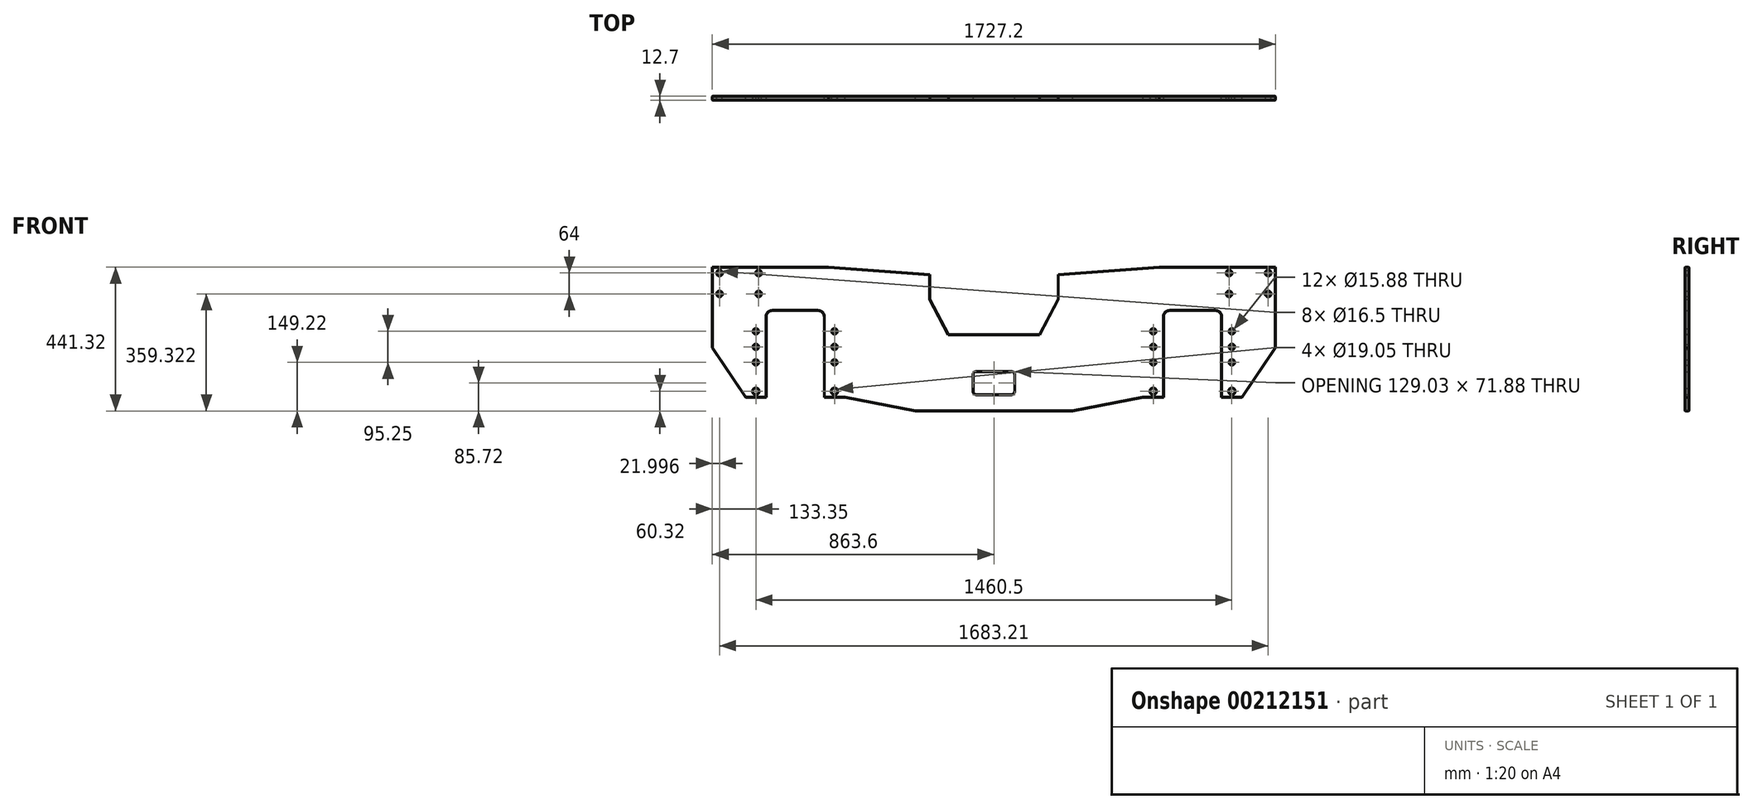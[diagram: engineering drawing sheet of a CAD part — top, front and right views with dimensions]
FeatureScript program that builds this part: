
annotation { "Feature Type Name" : "Feature", "Feature Type Description" : "" }
export const myFeature = defineFeature(function(context is Context, id is Id, definition is map)
    precondition{}
    {
        {
            var Q0;
            Q0=qCreatedBy(makeId("Front.planeOp"),FACE);
            var sketch = newSketch(context, id + "F0", { "sketchPlane" : qUnion([Q0])});
            skLineSegment(sketch, "E0", {"start": v(0, 0) * mm, "end": v(0, 247.15) * mm});
            skLineSegment(sketch, "E1", {"start": v(0, 247.15) * mm, "end": v(355.6, 247.15) * mm});
            skLineSegment(sketch, "E2", {"start": v(355.6, 247.15) * mm, "end": v(666.75, 224.93) * mm});
            skLineSegment(sketch, "E3", {"start": v(666.75, 224.93) * mm, "end": v(666.75, 148.73) * mm});
            skLineSegment(sketch, "E4", {"start": v(666.75, 148.73) * mm, "end": v(723.9, 40.78) * mm});
            skLineSegment(sketch, "E5", {"start": v(723.9, 40.78) * mm, "end": v(863.6, 40.78) * mm});
            skLineSegment(sketch, "E6", {"start": v(0, 0) * mm, "end": v(101.6, -152.9) * mm});
            skLineSegment(sketch, "E7", {"start": v(101.6, -152.9) * mm, "end": v(165.1, -152.9) * mm});
            skLineSegment(sketch, "E8", {"start": v(165.1, -152.9) * mm, "end": v(165.1, 94.75) * mm});
            skLineSegment(sketch, "E9", {"start": v(184.15, 113.8) * mm, "end": v(323.85, 113.8) * mm});
            skLineSegment(sketch, "E10", {"start": v(342.9, 94.75) * mm, "end": v(342.9, -152.9) * mm});
            skLineSegment(sketch, "E11", {"start": v(342.9, -152.9) * mm, "end": v(406.4, -152.9) * mm});
            skLineSegment(sketch, "E12", {"start": v(406.4, -152.9) * mm, "end": v(622.3, -194.17) * mm});
            skLineSegment(sketch, "E13", {"start": v(622.3, -194.17) * mm, "end": v(863.6, -194.17) * mm});
            skLineSegment(sketch, "E14", {"start": v(863.6, -194.17) * mm, "end": v(863.6, 40.78) * mm, "construction": true});
            skPoint(sketch, "E15.visualSharp", {"position": v(342.9, 113.8) * mm});
            skArc(sketch, "E15.filletArc", {"start": v(342.9, 94.75) * mm, "mid": v(337.32, 108.22) * mm, "end": v(323.85, 113.8) * mm});
            skPoint(sketch, "E16.visualSharp", {"position": v(165.1, 113.8) * mm});
            skArc(sketch, "E16.filletArc", {"start": v(184.15, 113.8) * mm, "mid": v(170.68, 108.22) * mm, "end": v(165.1, 94.75) * mm});
            skCircle(sketch, "E17", {"center": v(374.65, -133.85) * mm, "radius": 9.53 * mm});
            skCircle(sketch, "E18", {"center": v(133.35, -133.85) * mm, "radius": 9.53 * mm});
            skCircle(sketch, "E19", {"center": v(374.65, -44.95) * mm, "radius": 7.94 * mm});
            skCircle(sketch, "E20", {"center": v(374.65, 2.68) * mm, "radius": 7.94 * mm});
            skCircle(sketch, "E21", {"center": v(374.65, 50.3) * mm, "radius": 7.94 * mm});
            skCircle(sketch, "E22", {"center": v(133.35, -44.95) * mm, "radius": 7.94 * mm});
            skCircle(sketch, "E23", {"center": v(133.35, 2.68) * mm, "radius": 7.94 * mm});
            skCircle(sketch, "E24", {"center": v(133.35, 50.3) * mm, "radius": 7.94 * mm});
            skLineSegment(sketch, "E25.MirrorCS", {"start": v(1003.3, 40.78) * mm, "end": v(863.6, 40.78) * mm});
            skLineSegment(sketch, "E26.MirrorCS", {"start": v(1104.9, -194.17) * mm, "end": v(863.6, -194.17) * mm});
            skLineSegment(sketch, "E27.MirrorCS", {"start": v(1320.8, -152.9) * mm, "end": v(1104.9, -194.17) * mm});
            skLineSegment(sketch, "E28.MirrorCS", {"start": v(1384.3, -152.9) * mm, "end": v(1320.8, -152.9) * mm});
            skLineSegment(sketch, "E29.MirrorCS", {"start": v(1384.3, 94.75) * mm, "end": v(1384.3, -152.9) * mm});
            skArc(sketch, "E30.MirrorCS", {"start": v(1384.3, 94.75) * mm, "mid": v(1389.88, 108.22) * mm, "end": v(1403.35, 113.8) * mm});
            skLineSegment(sketch, "E31.MirrorCS", {"start": v(1543.05, 113.8) * mm, "end": v(1403.35, 113.8) * mm});
            skArc(sketch, "E32.MirrorCS", {"start": v(1543.05, 113.8) * mm, "mid": v(1556.52, 108.22) * mm, "end": v(1562.1, 94.75) * mm});
            skLineSegment(sketch, "E33.MirrorCS", {"start": v(1562.1, -152.9) * mm, "end": v(1562.1, 94.75) * mm});
            skLineSegment(sketch, "E34.MirrorCS", {"start": v(1625.6, -152.9) * mm, "end": v(1562.1, -152.9) * mm});
            skLineSegment(sketch, "E35.MirrorCS", {"start": v(1727.2, 0) * mm, "end": v(1625.6, -152.9) * mm});
            skLineSegment(sketch, "E36.MirrorCS", {"start": v(1727.2, 0) * mm, "end": v(1727.2, 247.15) * mm});
            skLineSegment(sketch, "E37.MirrorCS", {"start": v(1727.2, 247.15) * mm, "end": v(1371.6, 247.15) * mm});
            skLineSegment(sketch, "E38.MirrorCS", {"start": v(1371.6, 247.15) * mm, "end": v(1060.45, 224.93) * mm});
            skLineSegment(sketch, "E39.MirrorCS", {"start": v(1060.45, 224.93) * mm, "end": v(1060.45, 148.73) * mm});
            skLineSegment(sketch, "E40.MirrorCS", {"start": v(1060.45, 148.73) * mm, "end": v(1003.3, 40.78) * mm});
            skCircle(sketch, "E41.MirrorC", {"center": v(1352.55, -133.85) * mm, "radius": 9.53 * mm});
            skCircle(sketch, "E42.MirrorC", {"center": v(1352.55, -44.95) * mm, "radius": 7.94 * mm});
            skCircle(sketch, "E43.MirrorC", {"center": v(1352.55, 2.68) * mm, "radius": 7.94 * mm});
            skCircle(sketch, "E44.MirrorC", {"center": v(1352.55, 50.3) * mm, "radius": 7.94 * mm});
            skCircle(sketch, "E45.MirrorC", {"center": v(1593.85, 50.3) * mm, "radius": 7.94 * mm});
            skCircle(sketch, "E46.MirrorC", {"center": v(1593.85, 2.68) * mm, "radius": 7.94 * mm});
            skCircle(sketch, "E47.MirrorC", {"center": v(1593.85, -44.95) * mm, "radius": 7.94 * mm});
            skCircle(sketch, "E48.MirrorC", {"center": v(1593.85, -133.85) * mm, "radius": 9.53 * mm});
            skLineSegment(sketch, "E49.bottom", {"start": v(809.63, -73.52) * mm, "end": v(917.58, -73.52) * mm});
            skLineSegment(sketch, "E49.top", {"start": v(809.63, -143.37) * mm, "end": v(917.58, -143.37) * mm});
            skLineSegment(sketch, "E49.left", {"start": v(800.1, -83.05) * mm, "end": v(800.1, -133.85) * mm});
            skLineSegment(sketch, "E49.right", {"start": v(927.1, -83.05) * mm, "end": v(927.1, -133.85) * mm});
            skPoint(sketch, "E49.middle", {"position": v(863.6, -108.45) * mm});
            skPoint(sketch, "E50.visualSharp", {"position": v(800.1, -73.52) * mm});
            skArc(sketch, "E50.filletArc", {"start": v(809.63, -73.52) * mm, "mid": v(802.89, -76.31) * mm, "end": v(800.1, -83.05) * mm});
            skPoint(sketch, "E51.visualSharp", {"position": v(927.1, -73.52) * mm});
            skArc(sketch, "E51.filletArc", {"start": v(927.1, -83.05) * mm, "mid": v(924.31, -76.31) * mm, "end": v(917.58, -73.52) * mm});
            skPoint(sketch, "E52.visualSharp", {"position": v(927.1, -143.37) * mm});
            skArc(sketch, "E52.filletArc", {"start": v(917.58, -143.37) * mm, "mid": v(924.31, -140.58) * mm, "end": v(927.1, -133.85) * mm});
            skPoint(sketch, "E53.visualSharp", {"position": v(800.1, -143.37) * mm});
            skArc(sketch, "E53.filletArc", {"start": v(800.1, -133.85) * mm, "mid": v(802.89, -140.58) * mm, "end": v(809.63, -143.37) * mm});
            skCircle(sketch, "E54", {"center": v(22, 229.15) * mm, "radius": 8.25 * mm});
            skCircle(sketch, "E55", {"center": v(141.99, 229.15) * mm, "radius": 8.25 * mm});
            skCircle(sketch, "E56", {"center": v(141.99, 165.15) * mm, "radius": 8.25 * mm});
            skCircle(sketch, "E57", {"center": v(22, 165.15) * mm, "radius": 8.25 * mm});
            skCircle(sketch, "E58.MirrorC", {"center": v(1585.21, 229.15) * mm, "radius": 8.25 * mm});
            skCircle(sketch, "E59.MirrorC", {"center": v(1585.21, 165.15) * mm, "radius": 8.25 * mm});
            skCircle(sketch, "E60.MirrorC", {"center": v(1705.2, 165.15) * mm, "radius": 8.25 * mm});
            skCircle(sketch, "E61.MirrorC", {"center": v(1705.2, 229.15) * mm, "radius": 8.25 * mm});
            skSolve(sketch);
        }
        {
            var Q0;
            Q0=makeQuery(id+"F0.imprint","IMPRINT",FACE,{"disambiguationData":[TD([[makeQuery(id+"F0.imprint","IMPRINT",EDGE,{"derivedFrom":sQuery(id+"F0.wireOp",EDGE,"E0")}),-1.0]])]});
            extrude(context, id + "F1", {"entities" : qUnion([Q0]), "depth" : 12.7 * mm});
        }
        {
            var Q0;
            Q0=makeQuery(id+"F1.opExtrude","CAP_FACE",FACE,{"disambiguationData":[OSD([sQuery(id+"F0.wireOp",EDGE,"E0"),sQuery(id+"F0.wireOp",EDGE,"E1"),sQuery(id+"F0.wireOp",EDGE,"E2"),sQuery(id+"F0.wireOp",EDGE,"E3"),sQuery(id+"F0.wireOp",EDGE,"E4"),sQuery(id+"F0.wireOp",EDGE,"E5"),sQuery(id+"F0.wireOp",EDGE,"E6"),sQuery(id+"F0.wireOp",EDGE,"E7"),sQuery(id+"F0.wireOp",EDGE,"E8"),sQuery(id+"F0.wireOp",EDGE,"E9"),sQuery(id+"F0.wireOp",EDGE,"E10"),sQuery(id+"F0.wireOp",EDGE,"E11"),sQuery(id+"F0.wireOp",EDGE,"E12"),sQuery(id+"F0.wireOp",EDGE,"E13"),sQuery(id+"F0.wireOp",EDGE,"E15.filletArc"),sQuery(id+"F0.wireOp",EDGE,"E16.filletArc"),sQuery(id+"F0.wireOp",EDGE,"E17"),sQuery(id+"F0.wireOp",EDGE,"E18"),sQuery(id+"F0.wireOp",EDGE,"E19"),sQuery(id+"F0.wireOp",EDGE,"E20"),sQuery(id+"F0.wireOp",EDGE,"E21"),sQuery(id+"F0.wireOp",EDGE,"E22"),sQuery(id+"F0.wireOp",EDGE,"E23"),sQuery(id+"F0.wireOp",EDGE,"E24"),sQuery(id+"F0.wireOp",EDGE,"E25.MirrorCS"),sQuery(id+"F0.wireOp",EDGE,"E26.MirrorCS"),sQuery(id+"F0.wireOp",EDGE,"E27.MirrorCS"),sQuery(id+"F0.wireOp",EDGE,"E28.MirrorCS"),sQuery(id+"F0.wireOp",EDGE,"E29.MirrorCS"),sQuery(id+"F0.wireOp",EDGE,"E30.MirrorCS"),sQuery(id+"F0.wireOp",EDGE,"E31.MirrorCS"),sQuery(id+"F0.wireOp",EDGE,"E32.MirrorCS"),sQuery(id+"F0.wireOp",EDGE,"E33.MirrorCS"),sQuery(id+"F0.wireOp",EDGE,"E34.MirrorCS"),sQuery(id+"F0.wireOp",EDGE,"E35.MirrorCS"),sQuery(id+"F0.wireOp",EDGE,"E36.MirrorCS"),sQuery(id+"F0.wireOp",EDGE,"E37.MirrorCS"),sQuery(id+"F0.wireOp",EDGE,"E38.MirrorCS"),sQuery(id+"F0.wireOp",EDGE,"E39.MirrorCS"),sQuery(id+"F0.wireOp",EDGE,"E40.MirrorCS"),sQuery(id+"F0.wireOp",EDGE,"E41.MirrorC"),sQuery(id+"F0.wireOp",EDGE,"E42.MirrorC"),sQuery(id+"F0.wireOp",EDGE,"E43.MirrorC"),sQuery(id+"F0.wireOp",EDGE,"E44.MirrorC"),sQuery(id+"F0.wireOp",EDGE,"E45.MirrorC"),sQuery(id+"F0.wireOp",EDGE,"E46.MirrorC"),sQuery(id+"F0.wireOp",EDGE,"E47.MirrorC"),sQuery(id+"F0.wireOp",EDGE,"E48.MirrorC"),sQuery(id+"F0.wireOp",EDGE,"E49.bottom"),sQuery(id+"F0.wireOp",EDGE,"E49.top"),sQuery(id+"F0.wireOp",EDGE,"E49.left"),sQuery(id+"F0.wireOp",EDGE,"E49.right"),sQuery(id+"F0.wireOp",EDGE,"E50.filletArc"),sQuery(id+"F0.wireOp",EDGE,"E51.filletArc"),sQuery(id+"F0.wireOp",EDGE,"E52.filletArc"),sQuery(id+"F0.wireOp",EDGE,"E53.filletArc"),sQuery(id+"F0.wireOp",EDGE,"E54"),sQuery(id+"F0.wireOp",EDGE,"E55"),sQuery(id+"F0.wireOp",EDGE,"E56"),sQuery(id+"F0.wireOp",EDGE,"E57"),sQuery(id+"F0.wireOp",EDGE,"E58.MirrorC"),sQuery(id+"F0.wireOp",EDGE,"E59.MirrorC"),sQuery(id+"F0.wireOp",EDGE,"E60.MirrorC"),sQuery(id+"F0.wireOp",EDGE,"E61.MirrorC")])],"isStart":false});
            var Q1;
            Q1=makeQuery(id+"F1.opExtrude","CAP_FACE",FACE,{"disambiguationData":[OSD([sQuery(id+"F0.wireOp",EDGE,"E0"),sQuery(id+"F0.wireOp",EDGE,"E1"),sQuery(id+"F0.wireOp",EDGE,"E2"),sQuery(id+"F0.wireOp",EDGE,"E3"),sQuery(id+"F0.wireOp",EDGE,"E4"),sQuery(id+"F0.wireOp",EDGE,"E5"),sQuery(id+"F0.wireOp",EDGE,"E6"),sQuery(id+"F0.wireOp",EDGE,"E7"),sQuery(id+"F0.wireOp",EDGE,"E8"),sQuery(id+"F0.wireOp",EDGE,"E9"),sQuery(id+"F0.wireOp",EDGE,"E10"),sQuery(id+"F0.wireOp",EDGE,"E11"),sQuery(id+"F0.wireOp",EDGE,"E12"),sQuery(id+"F0.wireOp",EDGE,"E13"),sQuery(id+"F0.wireOp",EDGE,"E15.filletArc"),sQuery(id+"F0.wireOp",EDGE,"E16.filletArc"),sQuery(id+"F0.wireOp",EDGE,"E17"),sQuery(id+"F0.wireOp",EDGE,"E18"),sQuery(id+"F0.wireOp",EDGE,"E19"),sQuery(id+"F0.wireOp",EDGE,"E20"),sQuery(id+"F0.wireOp",EDGE,"E21"),sQuery(id+"F0.wireOp",EDGE,"E22"),sQuery(id+"F0.wireOp",EDGE,"E23"),sQuery(id+"F0.wireOp",EDGE,"E24"),sQuery(id+"F0.wireOp",EDGE,"E25.MirrorCS"),sQuery(id+"F0.wireOp",EDGE,"E26.MirrorCS"),sQuery(id+"F0.wireOp",EDGE,"E27.MirrorCS"),sQuery(id+"F0.wireOp",EDGE,"E28.MirrorCS"),sQuery(id+"F0.wireOp",EDGE,"E29.MirrorCS"),sQuery(id+"F0.wireOp",EDGE,"E30.MirrorCS"),sQuery(id+"F0.wireOp",EDGE,"E31.MirrorCS"),sQuery(id+"F0.wireOp",EDGE,"E32.MirrorCS"),sQuery(id+"F0.wireOp",EDGE,"E33.MirrorCS"),sQuery(id+"F0.wireOp",EDGE,"E34.MirrorCS"),sQuery(id+"F0.wireOp",EDGE,"E35.MirrorCS"),sQuery(id+"F0.wireOp",EDGE,"E36.MirrorCS"),sQuery(id+"F0.wireOp",EDGE,"E37.MirrorCS"),sQuery(id+"F0.wireOp",EDGE,"E38.MirrorCS"),sQuery(id+"F0.wireOp",EDGE,"E39.MirrorCS"),sQuery(id+"F0.wireOp",EDGE,"E40.MirrorCS"),sQuery(id+"F0.wireOp",EDGE,"E41.MirrorC"),sQuery(id+"F0.wireOp",EDGE,"E42.MirrorC"),sQuery(id+"F0.wireOp",EDGE,"E43.MirrorC"),sQuery(id+"F0.wireOp",EDGE,"E44.MirrorC"),sQuery(id+"F0.wireOp",EDGE,"E45.MirrorC"),sQuery(id+"F0.wireOp",EDGE,"E46.MirrorC"),sQuery(id+"F0.wireOp",EDGE,"E47.MirrorC"),sQuery(id+"F0.wireOp",EDGE,"E48.MirrorC"),sQuery(id+"F0.wireOp",EDGE,"E49.bottom"),sQuery(id+"F0.wireOp",EDGE,"E49.top"),sQuery(id+"F0.wireOp",EDGE,"E49.left"),sQuery(id+"F0.wireOp",EDGE,"E49.right"),sQuery(id+"F0.wireOp",EDGE,"E50.filletArc"),sQuery(id+"F0.wireOp",EDGE,"E51.filletArc"),sQuery(id+"F0.wireOp",EDGE,"E52.filletArc"),sQuery(id+"F0.wireOp",EDGE,"E53.filletArc"),sQuery(id+"F0.wireOp",EDGE,"E54"),sQuery(id+"F0.wireOp",EDGE,"E55"),sQuery(id+"F0.wireOp",EDGE,"E56"),sQuery(id+"F0.wireOp",EDGE,"E57"),sQuery(id+"F0.wireOp",EDGE,"E58.MirrorC"),sQuery(id+"F0.wireOp",EDGE,"E59.MirrorC"),sQuery(id+"F0.wireOp",EDGE,"E60.MirrorC"),sQuery(id+"F0.wireOp",EDGE,"E61.MirrorC")])],"isStart":true});
            chamfer(context, id + "F2", {"entities" : qUnion([Q0, Q1]), "width" : 1.02 * mm, "tangentPropagation" : true});
        }
        {
            var Q0;
            Q0=makeQuery(id+"F1.opExtrude","CAP_FACE",FACE,{"disambiguationData":[OSD([sQuery(id+"F0.wireOp",EDGE,"E0"),sQuery(id+"F0.wireOp",EDGE,"E1"),sQuery(id+"F0.wireOp",EDGE,"E2"),sQuery(id+"F0.wireOp",EDGE,"E3"),sQuery(id+"F0.wireOp",EDGE,"E4"),sQuery(id+"F0.wireOp",EDGE,"E5"),sQuery(id+"F0.wireOp",EDGE,"E6"),sQuery(id+"F0.wireOp",EDGE,"E7"),sQuery(id+"F0.wireOp",EDGE,"E8"),sQuery(id+"F0.wireOp",EDGE,"E9"),sQuery(id+"F0.wireOp",EDGE,"E10"),sQuery(id+"F0.wireOp",EDGE,"E11"),sQuery(id+"F0.wireOp",EDGE,"E12"),sQuery(id+"F0.wireOp",EDGE,"E13"),sQuery(id+"F0.wireOp",EDGE,"E15.filletArc"),sQuery(id+"F0.wireOp",EDGE,"E16.filletArc"),sQuery(id+"F0.wireOp",EDGE,"E17"),sQuery(id+"F0.wireOp",EDGE,"E18"),sQuery(id+"F0.wireOp",EDGE,"E19"),sQuery(id+"F0.wireOp",EDGE,"E20"),sQuery(id+"F0.wireOp",EDGE,"E21"),sQuery(id+"F0.wireOp",EDGE,"E22"),sQuery(id+"F0.wireOp",EDGE,"E23"),sQuery(id+"F0.wireOp",EDGE,"E24"),sQuery(id+"F0.wireOp",EDGE,"E25.MirrorCS"),sQuery(id+"F0.wireOp",EDGE,"E26.MirrorCS"),sQuery(id+"F0.wireOp",EDGE,"E27.MirrorCS"),sQuery(id+"F0.wireOp",EDGE,"E28.MirrorCS"),sQuery(id+"F0.wireOp",EDGE,"E29.MirrorCS"),sQuery(id+"F0.wireOp",EDGE,"E30.MirrorCS"),sQuery(id+"F0.wireOp",EDGE,"E31.MirrorCS"),sQuery(id+"F0.wireOp",EDGE,"E32.MirrorCS"),sQuery(id+"F0.wireOp",EDGE,"E33.MirrorCS"),sQuery(id+"F0.wireOp",EDGE,"E34.MirrorCS"),sQuery(id+"F0.wireOp",EDGE,"E35.MirrorCS"),sQuery(id+"F0.wireOp",EDGE,"E36.MirrorCS"),sQuery(id+"F0.wireOp",EDGE,"E37.MirrorCS"),sQuery(id+"F0.wireOp",EDGE,"E38.MirrorCS"),sQuery(id+"F0.wireOp",EDGE,"E39.MirrorCS"),sQuery(id+"F0.wireOp",EDGE,"E40.MirrorCS"),sQuery(id+"F0.wireOp",EDGE,"E41.MirrorC"),sQuery(id+"F0.wireOp",EDGE,"E42.MirrorC"),sQuery(id+"F0.wireOp",EDGE,"E43.MirrorC"),sQuery(id+"F0.wireOp",EDGE,"E44.MirrorC"),sQuery(id+"F0.wireOp",EDGE,"E45.MirrorC"),sQuery(id+"F0.wireOp",EDGE,"E46.MirrorC"),sQuery(id+"F0.wireOp",EDGE,"E47.MirrorC"),sQuery(id+"F0.wireOp",EDGE,"E48.MirrorC"),sQuery(id+"F0.wireOp",EDGE,"E49.bottom"),sQuery(id+"F0.wireOp",EDGE,"E49.top"),sQuery(id+"F0.wireOp",EDGE,"E49.left"),sQuery(id+"F0.wireOp",EDGE,"E49.right"),sQuery(id+"F0.wireOp",EDGE,"E50.filletArc"),sQuery(id+"F0.wireOp",EDGE,"E51.filletArc"),sQuery(id+"F0.wireOp",EDGE,"E52.filletArc"),sQuery(id+"F0.wireOp",EDGE,"E53.filletArc"),sQuery(id+"F0.wireOp",EDGE,"E54"),sQuery(id+"F0.wireOp",EDGE,"E55"),sQuery(id+"F0.wireOp",EDGE,"E56"),sQuery(id+"F0.wireOp",EDGE,"E57"),sQuery(id+"F0.wireOp",EDGE,"E58.MirrorC"),sQuery(id+"F0.wireOp",EDGE,"E59.MirrorC"),sQuery(id+"F0.wireOp",EDGE,"E60.MirrorC"),sQuery(id+"F0.wireOp",EDGE,"E61.MirrorC")])],"isStart":false});
            var sketch = newSketch(context, id + "F3", { "sketchPlane" : qUnion([Q0])});
            skLineSegment(sketch, "E62", {"start": v(254, -152.9) * mm, "end": v(254, 97.3) * mm, "construction": true});
            skLineSegment(sketch, "E63", {"start": v(254, 18.55) * mm, "end": v(63.5, 18.55) * mm, "construction": true});
            skLineSegment(sketch, "E64", {"start": v(254, 18.55) * mm, "end": v(1473.2, 18.55) * mm, "construction": true});
            skLineSegment(sketch, "E65", {"start": v(1473.2, -152.9) * mm, "end": v(1473.2, 18.55) * mm, "construction": true});
            skLineSegment(sketch, "E66", {"start": v(1473.2, 18.55) * mm, "end": v(1663.7, 18.55) * mm, "construction": true});
            skLineSegment(sketch, "E67.0", {"start": v(1563.12, -152.9) * mm, "end": v(1383.28, -152.9) * mm, "construction": true});
            skLineSegment(sketch, "E68.0", {"start": v(164.08, -152.9) * mm, "end": v(343.92, -152.9) * mm, "construction": true});
            skLineSegment(sketch, "E69.0", {"start": v(1060.45, 225) * mm, "end": v(666.75, 225) * mm, "construction": true});
            skLineSegment(sketch, "E70.0", {"start": v(666.75, 225) * mm, "end": v(666.75, 186.9) * mm, "construction": true});
            skLineSegment(sketch, "E71.0", {"start": v(1060.45, 225) * mm, "end": v(1060.45, 186.9) * mm, "construction": true});
            skLineSegment(sketch, "E72", {"start": v(666.75, 186.9) * mm, "end": v(657.23, 186.9) * mm, "construction": true});
            skLineSegment(sketch, "E73", {"start": v(1060.45, 186.9) * mm, "end": v(1069.98, 186.9) * mm, "construction": true});
            skLineSegment(sketch, "E74.0", {"start": v(1003.3, -34.22) * mm, "end": v(723.9, -34.22) * mm, "construction": true});
            skLineSegment(sketch, "E75", {"start": v(1282.7, 18.55) * mm, "end": v(1282.7, -87.6) * mm, "construction": true});
            skLineSegment(sketch, "E76", {"start": v(444.5, 18.55) * mm, "end": v(444.5, -100.61) * mm, "construction": true});
            skSolve(sketch);
        }
    });
